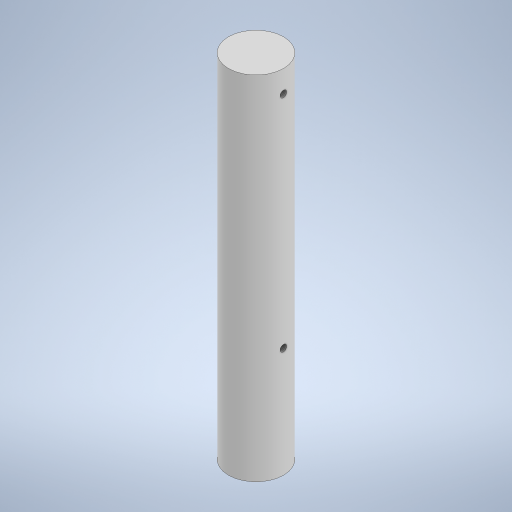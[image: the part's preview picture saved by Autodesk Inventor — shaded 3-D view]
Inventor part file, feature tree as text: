
AUTODESK INVENTOR PART (.ipt)
format: ipt  version: 2023 (Build 270158000, 158)  size: 252,928 bytes
history: native  units: mm
features: extrude x2, thread x2, sketch x2, other x1, hole x1
ambient origin geometry x8: Origin, YZ Plane, XZ Plane, XY Plane, X Axis, Y Axis, Z Axis, Center Point
bodies: Body1 (feature_tree)
feature tree (8):
  other  "Твердое тело1"
  extrude  "Выдавливание1"  Depth=25.0mm
  hole  "Отверстие1"  [1 undecoded]
  extrude  "Выдавливание3"  Depth=45.0mm
  thread  "Резьба4"
  thread  "Резьба5"
  sketch  "Эскиз1"
  sketch  "Эскиз2"
note: 1 required parameter value undecoded (feature->parameter linkage not recoverable at this tier; creation-order binding heuristic only, values carry confidence <= 0.55)
